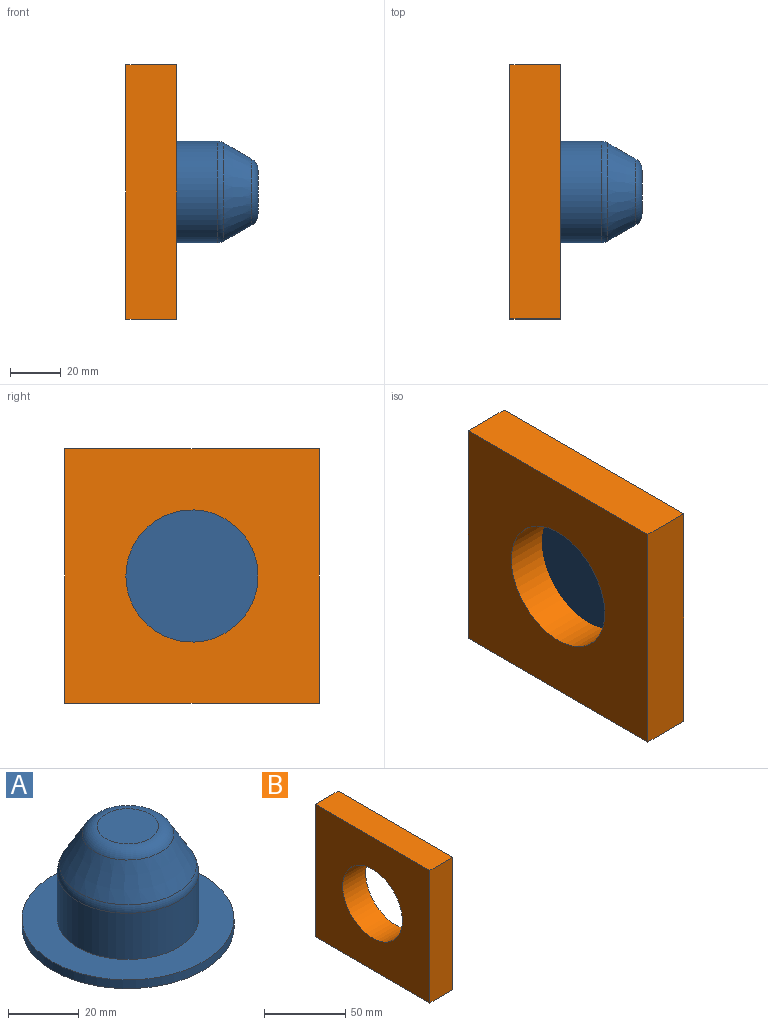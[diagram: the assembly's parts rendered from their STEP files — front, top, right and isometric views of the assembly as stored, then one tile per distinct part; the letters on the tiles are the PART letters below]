
ASSEMBLY  parts=2 mates=1
PART A: 8 faces, bbox 60x60x35 mm
  f0: plane 60x60mm, normal (0,0,1), area 1570.8mm2, adj f1,f7
  f1: cylinder r=20mm len=40mm, axis (0,0,-1), area 2010.6mm2, adj f0,f2
  f2: torus R=15mm, axis (0,0,-1), area 325.3mm2, adj f1,f3
  f3: cone r=12.98mm half-angle=30deg, axis (0,0,-1), area 1289.3mm2, adj f2,f4
  f4: torus R=8.65mm, axis (0,0,-1), area 363.1mm2, adj f3,f5
  f5: plane 17.3x17.3mm, normal (0,0,1), area 235mm2, adj f4
  f6: plane 60x60mm, normal (0,0,-1), area 2827.4mm2, adj f7
  f7: cylinder r=30mm len=60mm, axis (0,0,-1), area 565.5mm2, adj f0,f6
PART B: 7 faces, bbox 20x100x100 mm
  f0: plane 100x20mm, normal (0,0,-1), area 2000mm2, adj f1,f4,f5,f6
  f1: plane 100x20mm, normal (0,1,0), area 2000mm2, adj f0,f2,f5,f6
  f2: plane 100x20mm, normal (0,0,1), area 2000mm2, adj f1,f4,f5,f6
  f3: cylinder r=26mm len=52mm, axis (-1,0,0), area 3267.3mm2, adj f5,f6
  f4: plane 100x20mm, normal (0,-1,0), area 2000mm2, adj f0,f2,f5,f6
  f5: plane 100x100mm, normal (1,0,0), area 7876.3mm2, adj f0,f1,f2,f3,f4
  f6: plane 100x100mm, normal (-1,0,0), area 7876.3mm2, adj f0,f1,f2,f3,f4
PLACE A rot(axis=(0.71,0,0.71),180deg) t=(17,0,0)mm
PLACE B at identity
MATE fastened A.f1 <-> B.f3  axis (-1,0,0) through (20,0,0)mm
